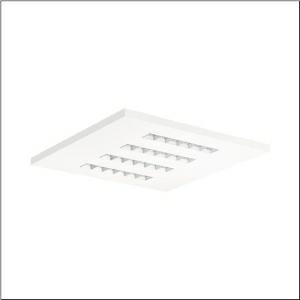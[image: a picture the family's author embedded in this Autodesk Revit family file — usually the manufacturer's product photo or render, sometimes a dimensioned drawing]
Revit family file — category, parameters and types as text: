
# Revit family: silica_r__21_square_51mx6mtut4w_6a14
name_source: partatom
category: Lighting Fixtures
units: mm (PartAtom-declared; Revit-internal decimal feet)

## family parameters
Cut with Voids When Loaded = No
Host = Face
Light Source = No
Part Type = Normal
Room Calculation Point = No
Round Connector Dimension = Use Diameter
Shared = No

## types (1)
- --- (1 x LED 2700 K ... 6500 K, 3720 lm, 30.7 W, 6500K)
    Apparent Load = 31 VA
    CIE Flux Codes = 81 98 100 100 100
    Color Rendering = 80
    Color Temperature = 6500K
    Default Elevation = 1800 mm
    Description = Silica® 21 Square, office luminaire, primary light control with lens, of PMMA, primary anti-glare with reflector, of PC, white, CAT 2 (L<= 3000cd/m²), light emission: direct distribution, primary light characteristic: symmetric, installation type: lay-in mounting, LED, rated luminous flux: 3.720lm, luminous efficacy: 113lm/W, light colour: 8tw, colour temperature: 2700..6500K, control gear: DALI-2 DT8, with terminal, 5-pole, mains connection: 220..240V, AC, 50/60Hz, rated input power: 32.8W, luminaire housing, of aluminium, traffic white (RAL 9016), module: M625, length: 622mm, width: 622mm, height: 32mm, protection rating (complete): IP20, insulation class (complete): insulation class I (protective earthing), certification: CE, ENEC, VDE, permissible operating ambient temperature: 0..+35°C, standard: EN 50419, packaging unit: 1 piece
    Height = 0 mm  [stored 0 ft]
    Lamp = 1 x LED 2700 K ... 6500 K
    Lamp Light Flux = 3720 lm
    Lamp Power = 30.7 W
    Lamp count = 1
    Length = 622 mm
    Luminous efficacy = 121 lm/W
    Manufacturer = Siteco
    ModVariant = No
    Model = 51MX6MTUT4W
    Mounting Place = Ceiling
    Mounting Type = Recessed
    Number of Poles = 1
    OnlyDefault = Yes
    Power Factor = 1
    Product Name = Silica® 21 Square
    Product group = office luminaire | ceiling recessed
    ProductGroupID = 401
    Protection Class = Protection class I
    Protection Degree = IP 20
    RLX_Detail_Level = 1
    RLX_Emergency_Light_Flux = 0 lm
    RLX_Emergency_Type = 0
    RLX_Emergency_Type_DB = No
    RlxData = <blob elided: 22461 chars, md5=98544ba6>
    Socket = socket
    Standby Power = 0 W
    System Light Flux = 3720 lm
    System Power = 31 W
    Type Comments = individual setting: CCT=6500K, colour temperature 6500K, luminous flux: 100 % | dim-lin: 254 | 381 mA
    Type Image = l_1275220.jpg
    URL = http://relux.com
    VarID = @adj_063950
    Voltage = 0 V
    Weight = 0.00 kg
    Width = 622 mm

note: [stored X ft] marks values corroborated as IEEE doubles in the binary element streams (Revit-internal decimal feet)

## geometry (parser evidence)
native form markers: Blend x4, Sweep x12
no freeform markers — native parametric forms only
